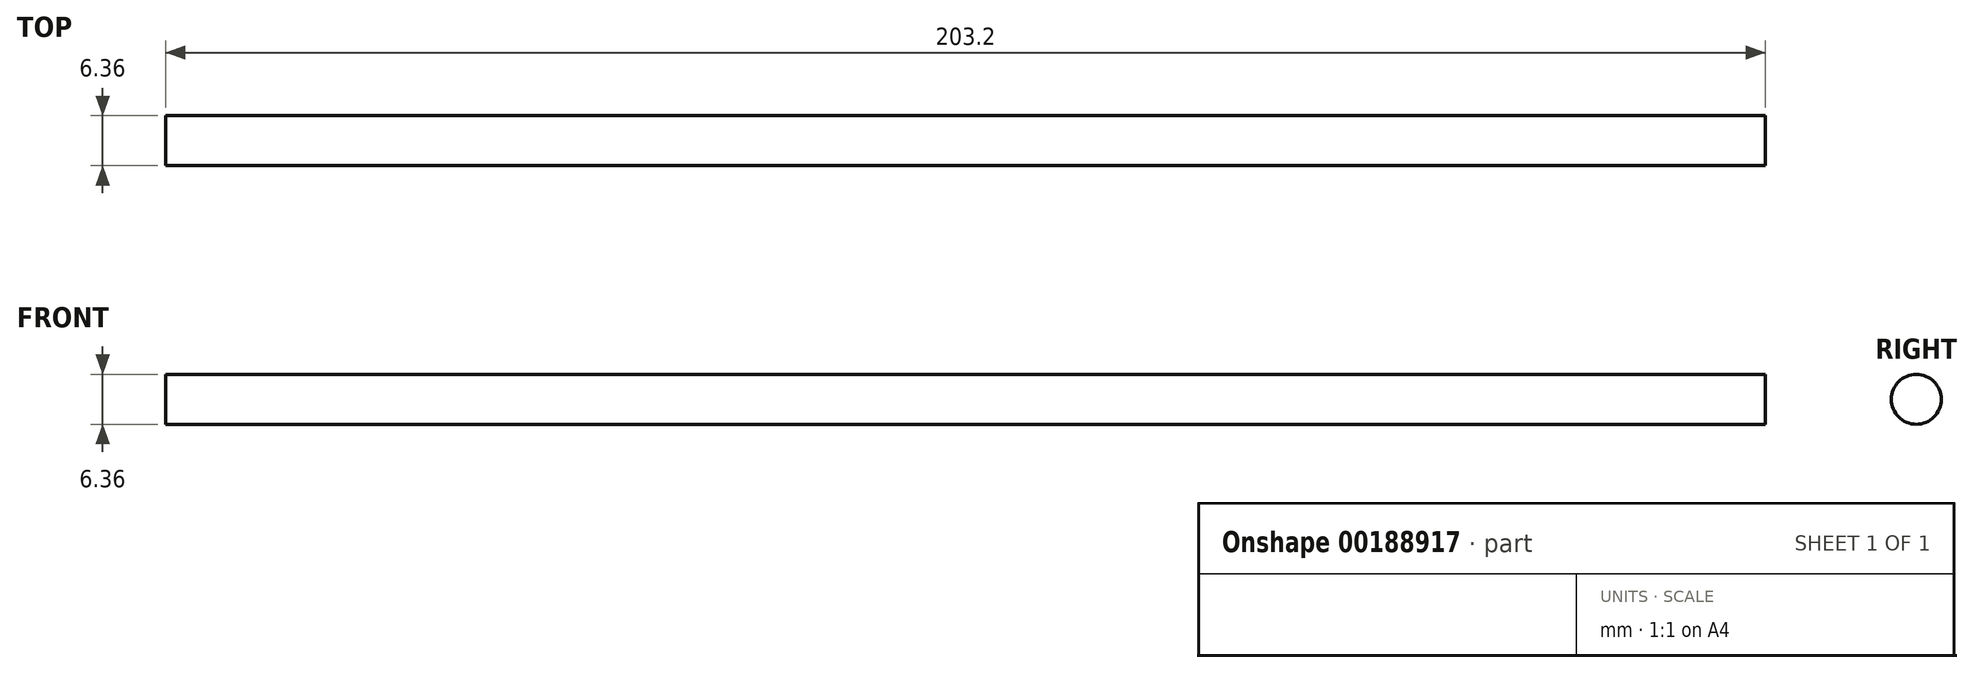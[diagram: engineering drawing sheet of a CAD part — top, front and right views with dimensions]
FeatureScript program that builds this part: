
annotation { "Feature Type Name" : "Feature", "Feature Type Description" : "" }
export const myFeature = defineFeature(function(context is Context, id is Id, definition is map)
    precondition{}
    {
        {
            var Q0;
            Q0=qCreatedBy(makeId("Right.planeOp"),FACE);
            var sketch = newSketch(context, id + "F0", { "sketchPlane" : qUnion([Q0])});
            skCircle(sketch, "E0", {"center": v(0, 0) * mm, "radius": 3.18 * mm});
            skSolve(sketch);
        }
        {
            var Q0;
            Q0=qSketchRegion(id+"F0",true);
            extrude(context, id + "F1", {"entities" : qUnion([Q0]), "depth" : 203.2 * mm});
        }
    });
